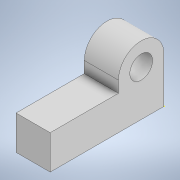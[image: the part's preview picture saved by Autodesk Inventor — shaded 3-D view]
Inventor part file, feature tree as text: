
AUTODESK INVENTOR PART (.ipt)
format: ipt  version: 2021 (Build 250183000, 183)  size: 121,344 bytes
history: native  units: mm
features: sketch x4, extrude x2, other x1, fillet x1, hole x1
ambient origin geometry x8: Origin, YZ Plane, XZ Plane, XY Plane, X Axis, Y Axis, Z Axis, Center Point
bodies: Body1 (feature_tree)
feature tree (9):
  other  "Sólido1"
  extrude  "Extrusão1"  Depth=100.0mm
  sketch  "Esboço2"  dims[d2=30.0mm d3=0.0mm d4=40.0mm d5=30.0mm d6=0.0mm]
  extrude  "Extrusão2"  Depth=40.0mm
  fillet  "Arredondamento2"  Radius=30.0mm
  hole  "Furo3"  [1 undecoded]
  sketch  "Esboço1"  dims[d0=30.0mm d1=100.0mm]
  sketch  "Esboço3"  dims[d26=20.0mm]
  sketch  "Esboço6"  dims[d27=20.0mm d28=6.0mm d29=4.0mm d30=2.0mm d31=90.0deg d32=8.0mm d33=20.594885mm d7=1.0mm d8=1.0mm d9=1.0mm d10=0.15mm d11=0.25mm d12=0.375mm d13=14.3117mm d14=0.75mm d15=20.594885mm d16=0.0625mm d17=0.75mm d18=0.375mm d19=0.15mm d20=0.25mm d21=0.375mm d22=14.3117mm d23=0.75mm d24=20.594885mm d25=0.0625mm]
note: 1 required parameter value undecoded (feature->parameter linkage not recoverable at this tier; creation-order binding heuristic only, values carry confidence <= 0.55)
